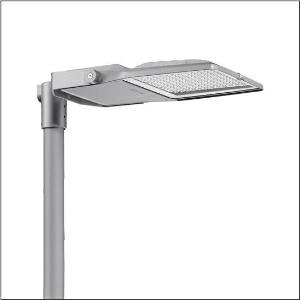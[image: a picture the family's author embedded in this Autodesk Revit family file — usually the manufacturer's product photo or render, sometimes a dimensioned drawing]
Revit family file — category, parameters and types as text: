
# Revit family: floodlight_fl_21_iq_midi___pl61_5xa7781f4c3a_8dc1
name_source: partatom
category: Lighting Fixtures
units: mm (PartAtom-declared; Revit-internal decimal feet)

## family parameters
Cut with Voids When Loaded = No
Host = Face
Light Source = No
Part Type = Normal
Room Calculation Point = No
Round Connector Dimension = Use Diameter
Shared = No

## types (1)
- --- (1 x LED, 36650 lm, 270.2 W, 4000K)
    Apparent Load = 270 VA
    CIE Flux Codes = 33 65 98 100 100
    Color Rendering = 70
    Color Temperature = 4000K
    Default Elevation = 1800 mm
    Description = Floodlight FL 21 iQ midi, floodlight, primary light control with lens, of PMMA, primary optical cover: protective disc, of toughened safety glass, transparent, light distribution: PL61, light emission: direct distribution, installation type: surface-mounted, LED, High Power LED, rated luminous flux: 36.650lm, luminous efficacy: 136lm/W, light colour: 740, colour temperature: 4000K, control gear: ECG iQ, control: optimised constant luminous flux control (CLO 2.0), Desk-Remote (wireless, voltage-free reading and setting of iQ features in the workshop via application-optimized NFC function/RFID function), Light-Fading, Smart-Wire, Night-Set, Lumen-Switch, Temp-Guard, Auto-Match, with terminal, 6-pole, mains connection: 220..240V, AC, 50/60Hz, start of lifetime: 270W, end of service life: 287W, reduction: 118W, luminaire housing, of diecast aluminium, powder-coated, Siteco® metallic grey (DB 702S), corrosivity category C5 mid according to DIN EN ISO 12944, sealing non-destructively replaceable, please order mast flange separately, mast bracket, of steel, galvanised, powder-coated, Siteco® metallic grey (DB 702S), protection rating (complete): IP66, insulation class (complete): insulation class II (safety insulation), certification: CE, ENEC, VDE, protection symbol: D, impact resistance: IK08, permissible operating ambient temperature: -40..+40°C, permissible operating ambient temperature for outdoor applications: -40..+50°C, standard: DIN EN 12944, LABS conformity tested according to VDMA 24364:2018-05, packaging unit: 1 piece

Light Distribution: PL61
    Height = 76 mm
    Lamp = 1 x LED
    Lamp Light Flux = 36650 lm
    Lamp Power = 270.2 W
    Lamp count = 1
    Length = 657 mm
    Luminous efficacy = 136 lm/W
    Manufacturer = Siteco
    ModVariant = No
    Model = 5XA7781F4C3A
    Number of Poles = 1
    OnlyDefault = Yes
    Power Factor = 1
    Product Name = Floodlight FL 21 iQ midi | PL61
    Product group = floodlight | pylon annexe
    ProductGroupID = 6200
    Protection Class = Protection class II
    Protection Degree = IP 66
    RLX_Detail_Level = 1
    RLX_Emergency_Light_Flux = 0 lm
    RLX_Emergency_Type = 0
    RLX_Emergency_Type_DB = No
    RlxData = <blob elided: 153821 chars, md5=a75a99d2>
    Socket = socket
    Standby Power = 0 W
    System Light Flux = 36650 lm
    System Power = 270 W
    Type Comments = factory setting: luminous flux: 100 % | dim-lin: 254 | 620 mA
    Type Image = l_1007123.jpg
    URL = http://relux.com
    VarID = @adj_077259
    Voltage = 0 V
    Weight = 0.00 kg
    Width = 442 mm

## geometry (parser evidence)
native form markers: Blend x4, Sweep x14
no freeform markers — native parametric forms only
